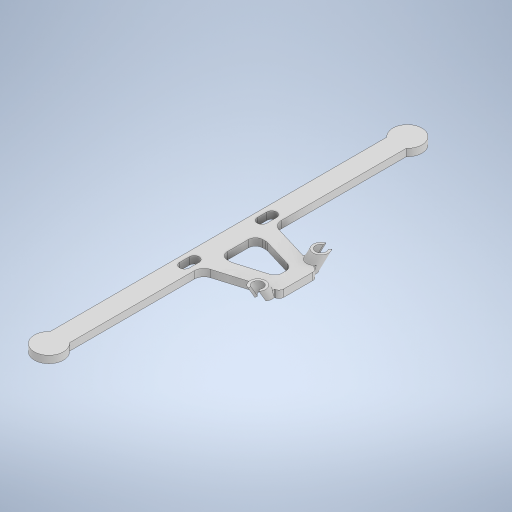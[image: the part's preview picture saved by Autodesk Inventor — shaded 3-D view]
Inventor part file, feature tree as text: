
AUTODESK INVENTOR PART (.ipt)
format: ipt  version: 2023.2 (Build 272271030, 271C)  size: 384,512 bytes
history: native  units: mm
features: sketch x3, fillet x3, sweep x3, extrude x1, plane x1, mirror x1
ambient origin geometry x8: Origin, YZ Plane, XZ Plane, XY Plane, X Axis, Y Axis, Z Axis, Center Point
bodies: Solid1 (feature_tree)
feature tree (12):
  sketch  "Sketch1"  dims[d2=12.0mm d5=16.0mm d9=15.0mm d11=7.5mm d12=6.4mm]
  extrude  "Extrusion1"  Depth=16.0mm
  fillet  "Fillet1"  Radius=15.0mm
  fillet  "Fillet2"  Radius=7.5mm
  fillet  "Fillet3"  Radius=6.4mm
  plane  "Work Plane2"
  sketch  "Sketch4"  dims[d13=4.4mm d14=2.0mm]
  sweep  "Sweep1"
  sweep  "Sweep2"
  sweep  "Sweep3"
  mirror  "Mirror5"
  sketch  "Sketch5"  dims[d15=6.0mm d16=3.0mm d17=0.0mm d18=4.0mm d19=4.0mm d20=3.0mm d25=25.307274mm d26=0.0mm d27=0.0mm d30=0.0mm d31=0.0mm d33=2.0mm d34=2.0mm d35=12.217305mm d36=0.0mm d37=0.0mm d28=0.872665mm d29=0.872665mm]
